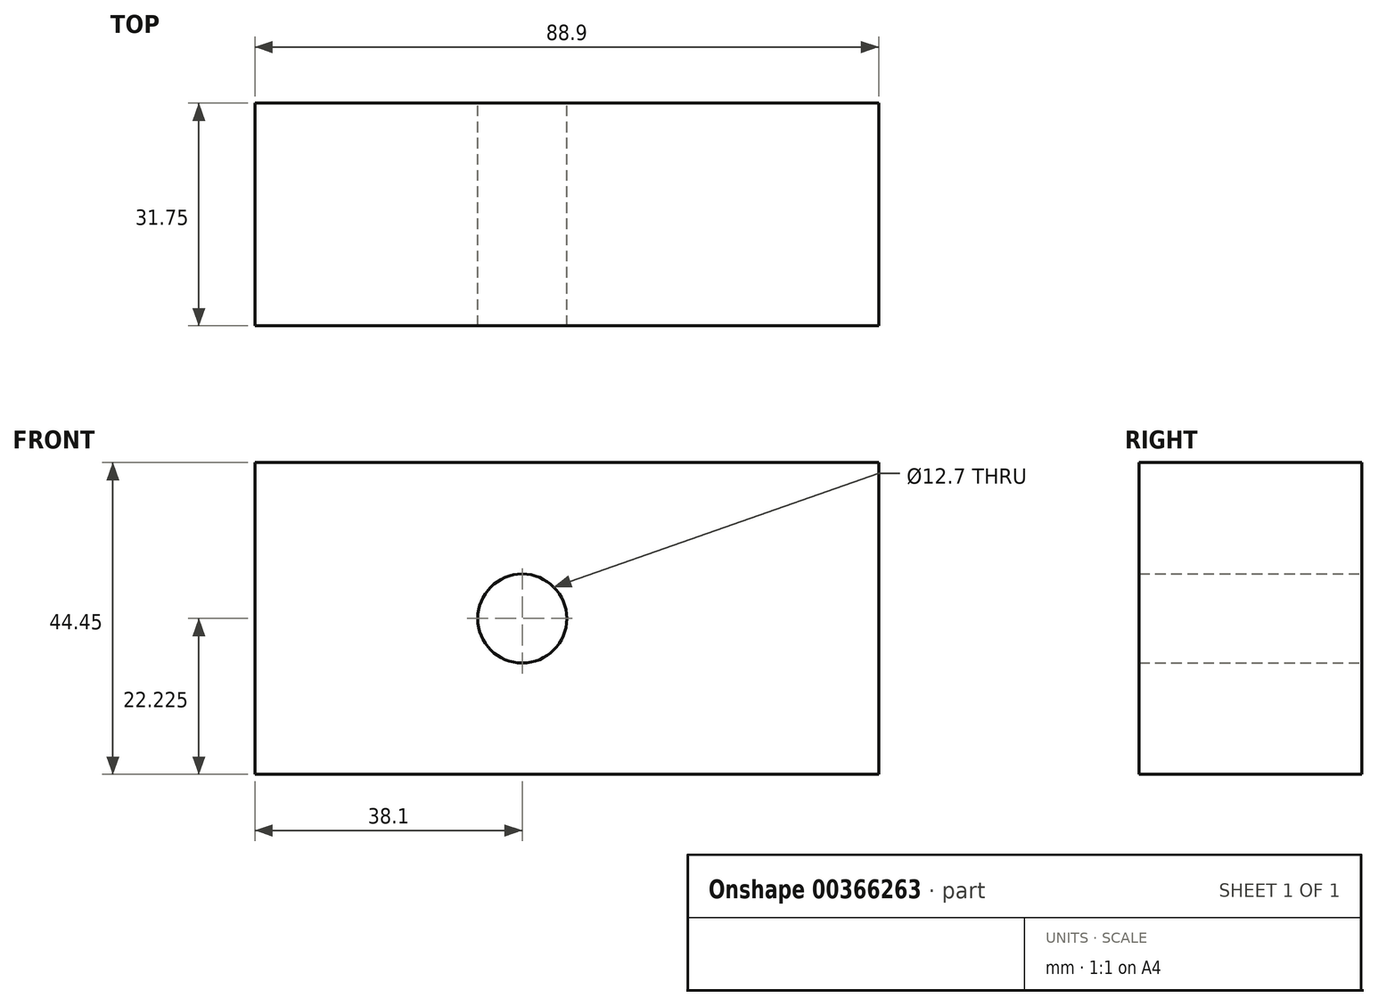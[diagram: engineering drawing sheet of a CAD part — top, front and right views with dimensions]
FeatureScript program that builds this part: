
annotation { "Feature Type Name" : "Feature", "Feature Type Description" : "" }
export const myFeature = defineFeature(function(context is Context, id is Id, definition is map)
    precondition{}
    {
        {
            var Q0;
            Q0=qCreatedBy(makeId("Front.planeOp"),FACE);
            var sketch = newSketch(context, id + "F0", { "sketchPlane" : qUnion([Q0])});
            skLineSegment(sketch, "E0", {"start": v(0, 0) * mm, "end": v(88.9, 0) * mm});
            skLineSegment(sketch, "E1", {"start": v(88.9, 0) * mm, "end": v(88.9, 44.45) * mm});
            skLineSegment(sketch, "E2", {"start": v(88.9, 44.45) * mm, "end": v(0, 44.45) * mm});
            skLineSegment(sketch, "E3", {"start": v(0, 44.45) * mm, "end": v(0, 0) * mm});
            skCircle(sketch, "E4", {"center": v(38.1, 22.23) * mm, "radius": 6.35 * mm});
            skSolve(sketch);
        }
        {
            var Q0;
            Q0 = qSketchRegion(id + "F0", true);
            extrude(context, id + "F1", {"entities" : qUnion([Q0]), "depth" : 31.75 * mm});
        }
    });
